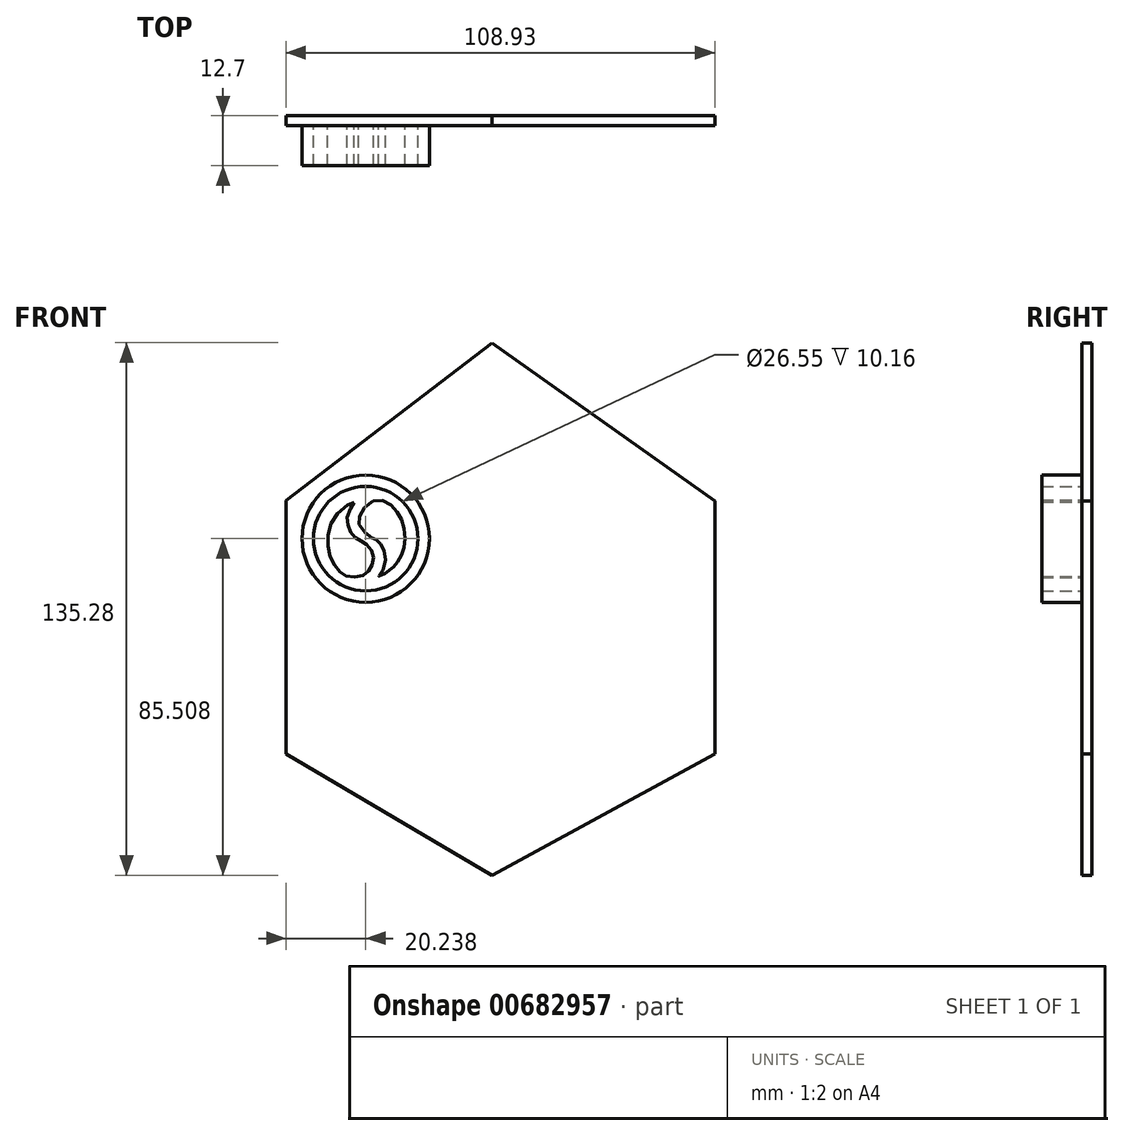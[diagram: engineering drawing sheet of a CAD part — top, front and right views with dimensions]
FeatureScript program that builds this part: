
annotation { "Feature Type Name" : "Feature", "Feature Type Description" : "" }
export const myFeature = defineFeature(function(context is Context, id is Id, definition is map)
    precondition{}
    {
        {
            var Q0;
            Q0=qCreatedBy(makeId("Front.planeOp"),FACE);
            var sketch = newSketch(context, id + "F0", { "sketchPlane" : qUnion([Q0])});
            skLineSegment(sketch, "E0", {"start": v(0, 68.56) * mm, "end": v(59.23, 26.56) * mm});
            skLineSegment(sketch, "E1", {"start": v(59.23, 26.56) * mm, "end": v(59.23, -40.56) * mm});
            skLineSegment(sketch, "E2", {"start": v(59.23, -40.56) * mm, "end": v(0, -72.79) * mm});
            skLineSegment(sketch, "E3", {"start": v(0, -72.79) * mm, "end": v(-54.78, -40.56) * mm});
            skLineSegment(sketch, "E4", {"start": v(-54.78, -40.56) * mm, "end": v(-54.78, 26.56) * mm});
            skLineSegment(sketch, "E5", {"start": v(-54.78, 26.56) * mm, "end": v(0, 68.56) * mm});
            skSolve(sketch);
        }
        {
            var Q0;
            Q0=makeQuery(id+"F0.imprint","IMPRINT",FACE,{"disambiguationData":[TD([[makeQuery(id+"F0.imprint","IMPRINT",EDGE,{"derivedFrom":sQuery(id+"F0.wireOp",EDGE,"E0")}),-1.0]])]});
            extrude(context, id + "F1", {"entities" : qUnion([Q0]), "depth" : 12.7 * mm, "offsetDistance" : 25.4 * mm});
        }
        {
            var Q0;
            Q0=makeQuery(id+"F1.opExtrude","CAP_FACE",FACE,{"disambiguationData":[OSD([sQuery(id+"F0.wireOp",EDGE,"E0"),sQuery(id+"F0.wireOp",EDGE,"E1"),sQuery(id+"F0.wireOp",EDGE,"E2"),sQuery(id+"F0.wireOp",EDGE,"E3"),sQuery(id+"F0.wireOp",EDGE,"E4"),sQuery(id+"F0.wireOp",EDGE,"E5")])],"isStart":false});
            extrude(context, id + "F2", {"entities" : qUnion([Q0]), "operationType" : NewBodyOperationType.REMOVE, "oppositeDirection" : true, "depth" : 2.54 * mm, "offsetDistance" : 25.4 * mm});
        }
        {
            var Q0;
            Q0=makeQuery(id+"F2.boolean.opBoolean","COPY",FACE,{"derivedFrom":makeQuery(id+"F2.opExtrude","CAP_FACE",FACE,{"disambiguationData":[OSD([sQuery(id+"F0.wireOp",EDGE,"E0"),sQuery(id+"F0.wireOp",EDGE,"E1"),sQuery(id+"F0.wireOp",EDGE,"E2"),sQuery(id+"F0.wireOp",EDGE,"E3"),sQuery(id+"F0.wireOp",EDGE,"E4"),sQuery(id+"F0.wireOp",EDGE,"E5")])],"isStart":false})});
            extrude(context, id + "F3", {"entities" : qUnion([Q0]), "operationType" : NewBodyOperationType.REMOVE, "oppositeDirection" : true, "depth" : 7.62 * mm, "offsetDistance" : 25.4 * mm});
        }
        {
            var Q0;
            Q0=makeQuery(id+"F1.opExtrude","SWEPT_FACE",FACE,{"disambiguationData":[OSD([sQuery(id+"F0.wireOp",EDGE,"E0")])]});
            extrude(context, id + "F4", {"entities" : qUnion([Q0]), "operationType" : NewBodyOperationType.REMOVE, "oppositeDirection" : true, "depth" : 2.54 * mm, "offsetDistance" : 25.4 * mm});
        }
        {
            var Q0;
            Q0=makeQuery(id+"F1.opExtrude","SWEPT_FACE",FACE,{"disambiguationData":[OSD([sQuery(id+"F0.wireOp",EDGE,"E5")])]});
            extrude(context, id + "F5", {"entities" : qUnion([Q0]), "operationType" : NewBodyOperationType.REMOVE, "oppositeDirection" : true, "depth" : 2.54 * mm, "offsetDistance" : 25.4 * mm});
        }
        {
            var Q0;
            Q0=makeQuery(id+"F1.opExtrude","SWEPT_FACE",FACE,{"disambiguationData":[OSD([sQuery(id+"F0.wireOp",EDGE,"E1")])]});
            extrude(context, id + "F6", {"entities" : qUnion([Q0]), "operationType" : NewBodyOperationType.REMOVE, "oppositeDirection" : true, "depth" : 2.54 * mm, "offsetDistance" : 25.4 * mm});
        }
        {
            var Q0;
            Q0=makeQuery(id+"F1.opExtrude","SWEPT_FACE",FACE,{"disambiguationData":[OSD([sQuery(id+"F0.wireOp",EDGE,"E4")])]});
            extrude(context, id + "F7", {"entities" : qUnion([Q0]), "operationType" : NewBodyOperationType.REMOVE, "oppositeDirection" : true, "depth" : 2.54 * mm, "offsetDistance" : 25.4 * mm});
        }
        {
            var Q0;
            Q0=makeQuery(id+"F1.opExtrude","SWEPT_FACE",FACE,{"disambiguationData":[OSD([sQuery(id+"F0.wireOp",EDGE,"E3")])]});
            extrude(context, id + "F8", {"entities" : qUnion([Q0]), "operationType" : NewBodyOperationType.REMOVE, "oppositeDirection" : true, "depth" : 2.54 * mm, "offsetDistance" : 25.4 * mm});
        }
        {
            var Q0;
            Q0=makeQuery(id+"F1.opExtrude","SWEPT_FACE",FACE,{"disambiguationData":[OSD([sQuery(id+"F0.wireOp",EDGE,"E2")])]});
            extrude(context, id + "F9", {"entities" : qUnion([Q0]), "operationType" : NewBodyOperationType.REMOVE, "oppositeDirection" : true, "depth" : 2.54 * mm, "offsetDistance" : 25.4 * mm});
        }
        {
            var Q0;
            Q0=makeQuery(id+"F3.boolean.opBoolean","COPY",FACE,{"derivedFrom":makeQuery(id+"F3.opExtrude","CAP_FACE",FACE,{"disambiguationData":[OSD([sQuery(id+"F0.wireOp",EDGE,"E0"),sQuery(id+"F0.wireOp",EDGE,"E1"),sQuery(id+"F0.wireOp",EDGE,"E2"),sQuery(id+"F0.wireOp",EDGE,"E3"),sQuery(id+"F0.wireOp",EDGE,"E4"),sQuery(id+"F0.wireOp",EDGE,"E5")])],"isStart":false})});
            var sketch = newSketch(context, id + "F10", { "sketchPlane" : qUnion([Q0])});
            skCircle(sketch, "E6", {"center": v(-32, 15.64) * mm, "radius": 13.27 * mm});
            skCircle(sketch, "E7", {"center": v(-32, 15.64) * mm, "radius": 16.17 * mm});
            skFitSpline(sketch, "E8", {"points": [v(-33.6, 21.24) * mm, v(-30.55, 25.02) * mm, v(-26.67, 24.9) * mm, v(-23.96, 22.34) * mm, v(-22.43, 19.2) * mm, v(-22.04, 14.93) * mm, v(-22.68, 12.03) * mm, v(-24.05, 9.56) * mm, v(-25.57, 7.85) * mm, v(-28.66, 6.08) * mm, v(-27.25, 8.4) * mm, v(-27.37, 12.55) * mm, v(-28.53, 14.62) * mm, v(-29.7, 15.6) * mm, v(-30.4, 15.78) * mm, v(-33.26, 18.53) * mm, v(-33.6, 21.24) * mm]});
            skFitSpline(sketch, "E9", {"points": [v(-34.98, 24.9) * mm, v(-38.62, 22.67) * mm, v(-41.47, 16.8) * mm, v(-41.11, 11.33) * mm, v(-38.99, 7.71) * mm, v(-36.78, 6.08) * mm, v(-33.32, 6.08) * mm, v(-31.19, 7.47) * mm, v(-30.13, 9.72) * mm, v(-30.24, 12.28) * mm, v(-32, 14.33) * mm, v(-33.67, 15.35) * mm, v(-35.56, 16.89) * mm, v(-36.47, 19.2) * mm, v(-36.55, 22) * mm, v(-34.98, 24.9) * mm]});
            skSolve(sketch);
        }
        {
            var Q0;
            Q0=makeQuery(id+"F10.imprint","IMPRINT",FACE,{"disambiguationData":[TD([[makeQuery(id+"F10.imprint","IMPRINT",EDGE,{"derivedFrom":sQuery(id+"F10.wireOp",EDGE,"E6")}),-1.0]])]});
            var Q1;
            Q1=makeQuery(id+"F10.imprint","IMPRINT",FACE,{"disambiguationData":[TD([[makeQuery(id+"F10.imprint","IMPRINT",EDGE,{"derivedFrom":sQuery(id+"F10.wireOp",EDGE,"E8")}),-1.0]])]});
            var Q2;
            Q2=makeQuery(id+"F10.imprint","IMPRINT",FACE,{"disambiguationData":[TD([[makeQuery(id+"F10.imprint","IMPRINT",EDGE,{"derivedFrom":sQuery(id+"F10.wireOp",EDGE,"E9")}),1.0]])]});
            extrude(context, id + "F11", {"entities" : qUnion([Q0, Q1, Q2]), "operationType" : NewBodyOperationType.ADD, "depth" : 10.16 * mm, "offsetDistance" : 25.4 * mm});
        }
    });
